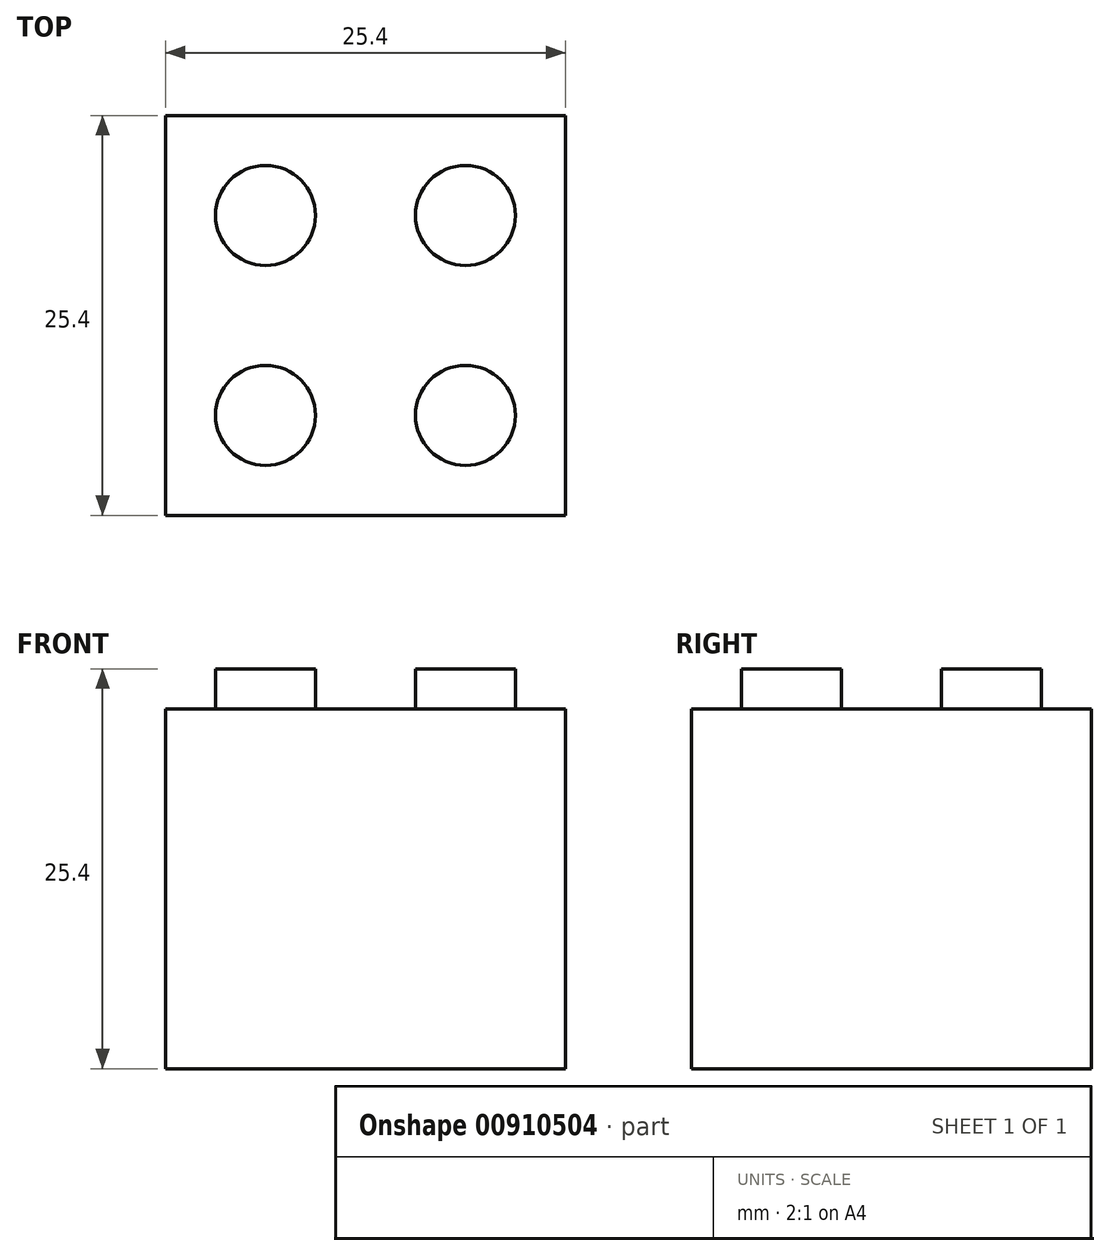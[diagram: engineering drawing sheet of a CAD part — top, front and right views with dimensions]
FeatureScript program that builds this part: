
annotation { "Feature Type Name" : "Feature", "Feature Type Description" : "" }
export const myFeature = defineFeature(function(context is Context, id is Id, definition is map)
    precondition{}
    {
        {
            var Q0;
            Q0=qCreatedBy(makeId("Top.planeOp"),FACE);
            var sketch = newSketch(context, id + "F0", { "sketchPlane" : qUnion([Q0])});
            skLineSegment(sketch, "E0.bottom", {"start": v(-51.1, 38.6) * mm, "end": v(-25.7, 38.6) * mm});
            skLineSegment(sketch, "E0.top", {"start": v(-51.1, 13.2) * mm, "end": v(-25.7, 13.2) * mm});
            skLineSegment(sketch, "E0.left", {"start": v(-51.1, 38.6) * mm, "end": v(-51.1, 13.2) * mm});
            skLineSegment(sketch, "E0.right", {"start": v(-25.7, 38.6) * mm, "end": v(-25.7, 13.2) * mm});
            skSolve(sketch);
        }
        {
            var Q0;
            Q0=makeQuery(id+"F0.imprint","IMPRINT",FACE,{"disambiguationData":[TD([[makeQuery(id+"F0.imprint","IMPRINT",EDGE,{"derivedFrom":sQuery(id+"F0.wireOp",EDGE,"E0.bottom")}),-1.0]])]});
            extrude(context, id + "F1", {"entities" : qUnion([Q0]), "depth" : 22.86 * mm, "offsetDistance" : 25.4 * mm});
        }
        {
            var Q0;
            Q0=makeQuery(id+"F1.opExtrude","CAP_FACE",FACE,{"disambiguationData":[OSD([sQuery(id+"F0.wireOp",EDGE,"E0.bottom"),sQuery(id+"F0.wireOp",EDGE,"E0.top"),sQuery(id+"F0.wireOp",EDGE,"E0.left"),sQuery(id+"F0.wireOp",EDGE,"E0.right")])],"isStart":false});
            var sketch = newSketch(context, id + "F2", { "sketchPlane" : qUnion([Q0])});
            skCircle(sketch, "E1", {"center": v(-44.75, 19.56) * mm, "radius": 3.18 * mm});
            skCircle(sketch, "E2", {"center": v(-44.75, 32.26) * mm, "radius": 3.18 * mm});
            skCircle(sketch, "E3", {"center": v(-32.05, 32.26) * mm, "radius": 3.18 * mm});
            skCircle(sketch, "E4", {"center": v(-32.05, 19.56) * mm, "radius": 3.18 * mm});
            skSolve(sketch);
        }
        {
            var Q0;
            Q0=makeQuery(id+"F2.imprint","IMPRINT",FACE,{"disambiguationData":[TD([[makeQuery(id+"F2.imprint","IMPRINT",EDGE,{"derivedFrom":sQuery(id+"F2.wireOp",EDGE,"E2")}),1.0]])]});
            var Q1;
            Q1=makeQuery(id+"F2.imprint","IMPRINT",FACE,{"disambiguationData":[TD([[makeQuery(id+"F2.imprint","IMPRINT",EDGE,{"derivedFrom":sQuery(id+"F2.wireOp",EDGE,"E1")}),1.0]])]});
            var Q2;
            Q2=makeQuery(id+"F2.imprint","IMPRINT",FACE,{"disambiguationData":[TD([[makeQuery(id+"F2.imprint","IMPRINT",EDGE,{"derivedFrom":sQuery(id+"F2.wireOp",EDGE,"E4")}),1.0]])]});
            var Q3;
            Q3=makeQuery(id+"F2.imprint","IMPRINT",FACE,{"disambiguationData":[TD([[makeQuery(id+"F2.imprint","IMPRINT",EDGE,{"derivedFrom":sQuery(id+"F2.wireOp",EDGE,"E3")}),1.0]])]});
            extrude(context, id + "F3", {"entities" : qUnion([Q0, Q1, Q2, Q3]), "operationType" : NewBodyOperationType.ADD, "depth" : 2.54 * mm, "offsetDistance" : 25.4 * mm});
        }
    });
